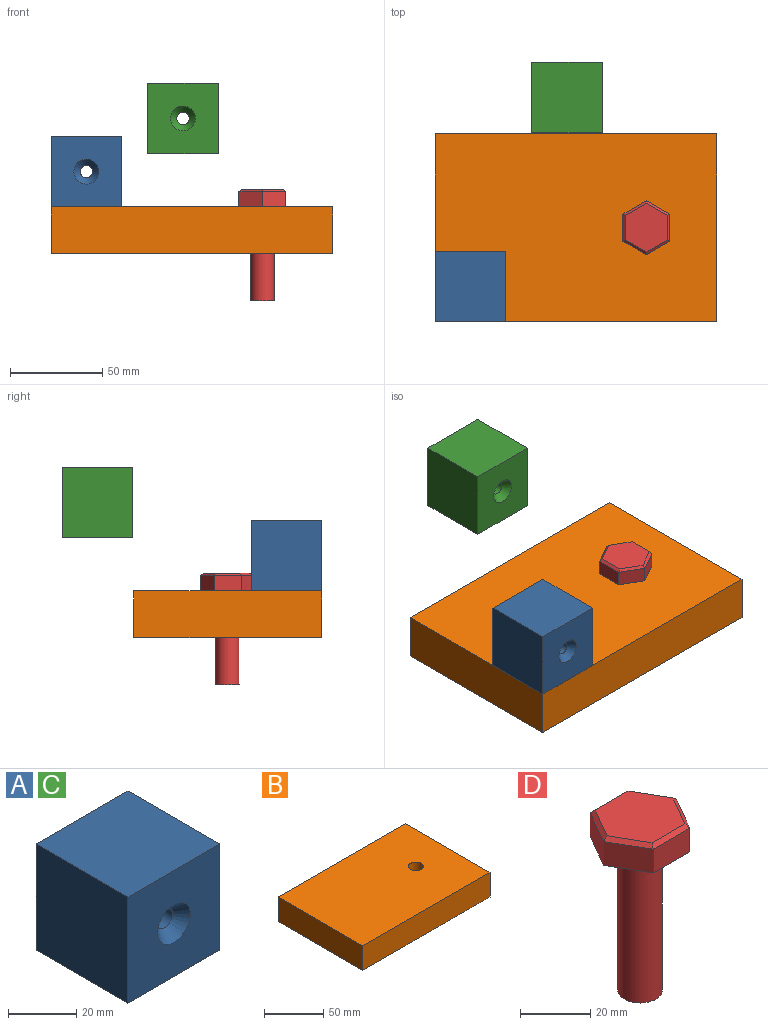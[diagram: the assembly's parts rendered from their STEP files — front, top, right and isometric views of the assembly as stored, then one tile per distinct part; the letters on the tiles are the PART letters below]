
ASSEMBLY  parts=4 mates=2
PART A: 8 faces, bbox 38.1x38.1x38.1 mm
  f0: plane 38.1x38.1mm, normal (1,0,0), area 1451.6mm2, adj f1,f3,f4,f5
  f1: plane 38.1x38.1mm, normal (0,1,0), area 1415.8mm2, adj f0,f2,f4,f5,f6
  f2: plane 38.1x38.1mm, normal (-1,0,0), area 1451.6mm2, adj f1,f3,f4,f5
  f3: plane 38.1x38.1mm, normal (0,-1,0), area 1308.7mm2, adj f0,f2,f4,f5,f7
  f4: plane 38.1x38.1mm, normal (0,0,1), area 1451.6mm2, adj f0,f1,f2,f3
  f5: plane 38.1x38.1mm, normal (0,0,-1), area 1451.6mm2, adj f0,f1,f2,f3
  f6: cylinder r=3.38mm len=34.23mm, axis (0,-1,0), area 726.5mm2, adj f1,f7
  f7: cone r=3.38mm half-angle=41deg, axis (0,-1,0), area 163.1mm2, adj f3,f6
PART B: 7 faces, bbox 152.4x101.6x25.4 mm
  f0: plane 101.6x25.4mm, normal (1,0,0), area 2580.6mm2, adj f1,f3,f5,f6
  f1: plane 152.4x25.4mm, normal (0,1,0), area 3871mm2, adj f0,f2,f5,f6
  f2: plane 101.6x25.4mm, normal (-1,0,0), area 2580.6mm2, adj f1,f3,f5,f6
  f3: plane 152.4x25.4mm, normal (0,-1,0), area 3871mm2, adj f0,f2,f5,f6
  f4: cylinder r=6.35mm len=25.4mm, axis (0,0,-1), area 1013.4mm2, adj f5,f6
  f5: plane 152.4x101.6mm, normal (0,0,1), area 15357.2mm2, adj f0,f1,f2,f3,f4
  f6: plane 152.4x101.6mm, normal (0,0,-1), area 15357.2mm2, adj f0,f1,f2,f3,f4
PART C: same geometry as A
PART D: 16 faces, bbox 29.3x25.4x60.3 mm
  f0: cylinder r=6.35mm len=50.8mm, axis (0,0,-1), area 2026.8mm2, adj f1,f9
  f1: plane 12.7x12.7mm, normal (0,0,-1), area 126.7mm2, adj f0
  f2: plane 12.7x8.26mm, normal (-0.87,-0.5,0), area 121.1mm2, adj f3,f7,f9,f15
  f3: plane 14.66x8.26mm, normal (0,-1,0), area 121.1mm2, adj f2,f4,f9,f13
  f4: plane 12.7x8.26mm, normal (0.87,-0.5,0), area 121.1mm2, adj f3,f5,f9,f11
  f5: plane 12.7x8.26mm, normal (0.87,0.5,0), area 121.1mm2, adj f4,f6,f9,f10
  f6: plane 14.66x8.26mm, normal (0,1,0), area 121.1mm2, adj f5,f7,f9,f12
  f7: plane 12.7x8.26mm, normal (-0.87,0.5,0), area 121.1mm2, adj f2,f6,f9,f14
  f8: plane 26.4x22.86mm, normal (0,0,1), area 452.6mm2, adj f10,f11,f12,f13,f14,f15
  f9: plane 29.33x25.4mm, normal (0,0,-1), area 432mm2, adj f0,f2,f3,f4,f5,f6,f7
  f10: plane 12.7x8.07mm, normal (0.61,0.35,0.71), area 25mm2, adj f5,f8,f11,f12
  f11: plane 12.7x8.07mm, normal (0.61,-0.35,0.71), area 25mm2, adj f4,f8,f10,f13
  f12: plane 14.66x1.27mm, normal (0,0.71,0.71), area 25mm2, adj f6,f8,f10,f14
  f13: plane 14.66x1.27mm, normal (0,-0.71,0.71), area 25mm2, adj f3,f8,f11,f15
  f14: plane 12.7x8.07mm, normal (-0.61,0.35,0.71), area 25mm2, adj f7,f8,f12,f15
  f15: plane 12.7x8.07mm, normal (-0.61,-0.35,0.71), area 25mm2, adj f2,f8,f13,f14
PLACE A t=(-57.15,-31.75,0)mm
PLACE B at identity fixed
PLACE C t=(-4.87,70.34,28.76)mm
PLACE D rot(axis=(0,0,1),90deg) t=(38.1,-38.1,-12.7)mm
MATE fastened A.f5 <-> B.f5  axis (0,0,1) through (-76.2,-50.8,12.7)mm
MATE fastened D.f0 <-> B.f4  axis (0,0,-1) through (38.1,0,12.7)mm
